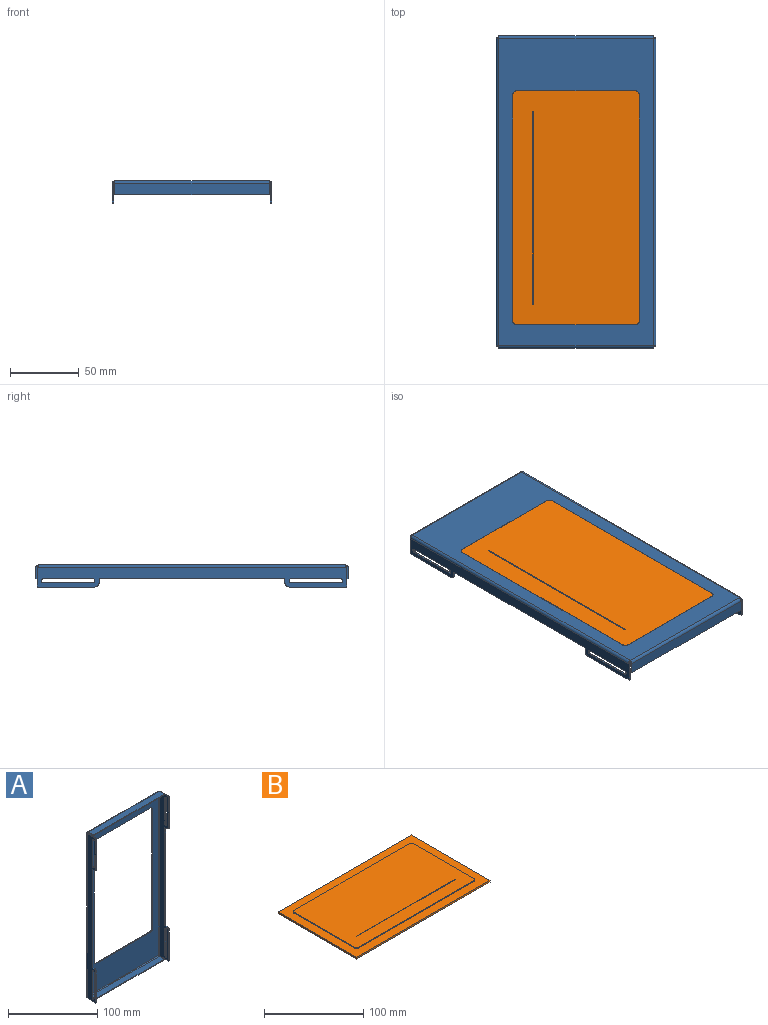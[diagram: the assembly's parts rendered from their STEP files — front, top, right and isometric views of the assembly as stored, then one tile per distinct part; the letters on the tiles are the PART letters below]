
ASSEMBLY  parts=2 mates=1
PART A: 78 faces, bbox 116x16x227 mm
  f0: cylinder r=3mm len=3mm, axis (0,1,0), area 4.7mm2, adj f1,f7,f8,f9
  f1: plane 86x1mm, normal (0,0,1), area 86mm2, adj f0,f2,f8,f9
  f2: cylinder r=3mm len=3mm, axis (0,1,0), area 4.7mm2, adj f1,f3,f8,f9
  f3: plane 164x1mm, normal (-1,0,0), area 164mm2, adj f2,f4,f8,f9
  f4: cylinder r=3mm len=3mm, axis (0,1,0), area 4.7mm2, adj f3,f5,f8,f9
  f5: plane 86x1mm, normal (0,0,-1), area 86mm2, adj f4,f6,f8,f9
  f6: cylinder r=3mm len=3mm, axis (0,1,0), area 4.7mm2, adj f5,f7,f8,f9
  f7: plane 164x1mm, normal (1,0,0), area 164mm2, adj f0,f6,f8,f9
  f8: plane 223x112mm, normal (0,1,0), area 9343.7mm2, adj f0,f1,f2,f3,f4,f5,f6,f7
  f9: plane 223x112mm, normal (0,-1,0), area 9343.7mm2, adj f0,f1,f2,f3,f4,f5,f6,f7
  f10: plane 1x1mm, normal (0,1,0), area 1mm2, adj f16,f29,f30,f32
  f11: plane 3x1mm, normal (0,0,1), area 3mm2, adj f12,f28,f29,f30
  f12: plane 135x1mm, normal (0,-1,0), area 135mm2, adj f11,f13,f29,f30
  f13: plane 3x1mm, normal (0,0,-1), area 3mm2, adj f12,f14,f29,f30
  f14: cylinder r=3mm len=3mm, axis (-1,0,0), area 4.7mm2, adj f13,f15,f29,f30
  f15: plane 42x1mm, normal (0,-1,0), area 42mm2, adj f14,f16,f29,f30
  f16: plane 14x1mm, normal (0,0,1), area 14mm2, adj f10,f15,f29,f30
  f17: plane 1x1mm, normal (0,1,0), area 1mm2, adj f18,f29,f30,f31
  f18: plane 14x1mm, normal (0,0,-1), area 14mm2, adj f17,f19,f29,f30
  f19: plane 42x1mm, normal (0,-1,0), area 42mm2, adj f18,f28,f29,f30
  f20: cylinder r=1.5mm len=3mm, axis (-1,0,0), area 4.7mm2, adj f21,f27,f29,f30
  f21: plane 36x1mm, normal (0,-1,0), area 36mm2, adj f20,f22,f29,f30
  f22: cylinder r=1.5mm len=3mm, axis (-1,0,0), area 4.7mm2, adj f21,f27,f29,f30
  f23: cylinder r=1.5mm len=3mm, axis (-1,0,0), area 4.7mm2, adj f24,f26,f29,f30
  f24: plane 36x1mm, normal (0,-1,0), area 36mm2, adj f23,f25,f29,f30
  f25: cylinder r=1.5mm len=3mm, axis (-1,0,0), area 4.7mm2, adj f24,f26,f29,f30
  f26: plane 36x1mm, normal (0,1,0), area 36mm2, adj f23,f25,f29,f30
  f27: plane 36x1mm, normal (0,1,0), area 36mm2, adj f20,f22,f29,f30
  f28: cylinder r=3mm len=3mm, axis (-1,0,0), area 4.7mm2, adj f11,f19,f29,f30
  f29: plane 225x14mm, normal (-1,0,0), area 2106mm2, adj f10,f11,f12,f13,f14,f15,f16,f17
  f30: plane 225x14mm, normal (1,0,0), area 2106mm2, adj f10,f11,f12,f13,f14,f15,f16,f17
  f31: plane 2x2mm, normal (0,0,-1), area 2.4mm2, adj f17,f33,f34,f65
  f32: plane 2x2mm, normal (0,0,1), area 2.4mm2, adj f10,f33,f34,f75
  f33: cylinder r=2mm len=223mm, axis (0,0,-1), area 700.6mm2, adj f8,f29,f31,f32
  f34: cylinder r=1mm len=223mm, axis (0,0,-1), area 350.3mm2, adj f9,f30,f31,f32
  f35: plane 1x1mm, normal (0,1,0), area 1mm2, adj f37,f54,f55,f57
  f36: plane 42x1mm, normal (0,-1,0), area 42mm2, adj f37,f53,f54,f55
  f37: plane 14x1mm, normal (0,0,-1), area 14mm2, adj f35,f36,f54,f55
  f38: plane 1x1mm, normal (0,1,0), area 1mm2, adj f39,f54,f55,f56
  f39: plane 14x1mm, normal (0,0,1), area 14mm2, adj f38,f40,f54,f55
  f40: plane 42x1mm, normal (0,-1,0), area 42mm2, adj f39,f41,f54,f55
  f41: cylinder r=3mm len=3mm, axis (1,0,0), area 4.7mm2, adj f40,f42,f54,f55
  f42: plane 3x1mm, normal (0,0,-1), area 3mm2, adj f41,f43,f54,f55
  f43: plane 135x1mm, normal (0,-1,0), area 135mm2, adj f42,f44,f54,f55
  f44: plane 3x1mm, normal (0,0,1), area 3mm2, adj f43,f53,f54,f55
  f45: cylinder r=1.5mm len=3mm, axis (1,0,0), area 4.7mm2, adj f46,f52,f54,f55
  f46: plane 36x1mm, normal (0,1,0), area 36mm2, adj f45,f47,f54,f55
  f47: cylinder r=1.5mm len=3mm, axis (1,0,0), area 4.7mm2, adj f46,f52,f54,f55
  f48: cylinder r=1.5mm len=3mm, axis (1,0,0), area 4.7mm2, adj f49,f51,f54,f55
  f49: plane 36x1mm, normal (0,1,0), area 36mm2, adj f48,f50,f54,f55
  f50: cylinder r=1.5mm len=3mm, axis (1,0,0), area 4.7mm2, adj f49,f51,f54,f55
  f51: plane 36x1mm, normal (0,-1,0), area 36mm2, adj f48,f50,f54,f55
  f52: plane 36x1mm, normal (0,-1,0), area 36mm2, adj f45,f47,f54,f55
  f53: cylinder r=3mm len=3mm, axis (1,0,0), area 4.7mm2, adj f36,f44,f54,f55
  f54: plane 225x14mm, normal (1,0,0), area 2106mm2, adj f35,f36,f37,f38,f39,f40,f41,f42
  f55: plane 225x14mm, normal (-1,0,0), area 2106mm2, adj f35,f36,f37,f38,f39,f40,f41,f42
  f56: plane 2x2mm, normal (0,0,1), area 2.4mm2, adj f38,f58,f59,f74
  f57: plane 2x2mm, normal (0,0,-1), area 2.4mm2, adj f35,f58,f59,f66
  f58: cylinder r=2mm len=223mm, axis (0,0,1), area 700.6mm2, adj f8,f54,f56,f57
  f59: cylinder r=1mm len=223mm, axis (0,0,1), area 350.3mm2, adj f9,f55,f56,f57
  f60: plane 8x1mm, normal (-1,0,0), area 8mm2, adj f62,f63,f64,f65
  f61: plane 8x1mm, normal (1,0,0), area 8mm2, adj f62,f63,f64,f66
  f62: plane 112x1mm, normal (0,-1,0), area 112mm2, adj f60,f61,f63,f64
  f63: plane 112x8mm, normal (0,0,-1), area 896mm2, adj f60,f61,f62,f67
  f64: plane 112x8mm, normal (0,0,1), area 896mm2, adj f60,f61,f62,f68
  f65: plane 2x2mm, normal (-1,0,0), area 2.4mm2, adj f31,f60,f67,f68
  f66: plane 2x2mm, normal (1,0,0), area 2.4mm2, adj f57,f61,f67,f68
  f67: cylinder r=2mm len=112mm, axis (-1,0,0), area 351.9mm2, adj f8,f63,f65,f66
  f68: cylinder r=1mm len=112mm, axis (-1,0,0), area 175.9mm2, adj f9,f64,f65,f66
  f69: plane 8x1mm, normal (1,0,0), area 8mm2, adj f71,f72,f73,f74
  f70: plane 8x1mm, normal (-1,0,0), area 8mm2, adj f71,f72,f73,f75
  f71: plane 112x1mm, normal (0,-1,0), area 112mm2, adj f69,f70,f72,f73
  f72: plane 112x8mm, normal (0,0,1), area 896mm2, adj f69,f70,f71,f76
  f73: plane 112x8mm, normal (0,0,-1), area 896mm2, adj f69,f70,f71,f77
  f74: plane 2x2mm, normal (1,0,0), area 2.4mm2, adj f56,f69,f76,f77
  f75: plane 2x2mm, normal (-1,0,0), area 2.4mm2, adj f32,f70,f76,f77
  f76: cylinder r=2mm len=112mm, axis (1,0,0), area 351.9mm2, adj f8,f72,f74,f75
  f77: cylinder r=1mm len=112mm, axis (1,0,0), area 175.9mm2, adj f9,f73,f74,f75
PART B: 27 faces, bbox 190x112x3 mm
  f0: plane 190x2mm, normal (0,-1,0), area 380mm2, adj f1,f3,f4,f13
  f1: plane 112x2mm, normal (1,0,0), area 224mm2, adj f0,f2,f4,f13
  f2: plane 190x2mm, normal (0,1,0), area 380mm2, adj f1,f3,f4,f13
  f3: plane 112x2mm, normal (-1,0,0), area 224mm2, adj f0,f2,f4,f13
  f4: plane 190x112mm, normal (0,0,-1), area 21280mm2, adj f0,f1,f2,f3
  f5: cylinder r=3mm len=3mm, axis (0,0,1), area 4.2mm2, adj f6,f12,f13,f22
  f6: plane 164x0.9mm, normal (0,-1,0), area 147.6mm2, adj f5,f7,f13,f20
  f7: cylinder r=3mm len=3mm, axis (0,0,1), area 4.2mm2, adj f6,f8,f13,f18
  f8: plane 86x0.9mm, normal (-1,0,0), area 77.4mm2, adj f7,f9,f13,f16
  f9: cylinder r=3mm len=3mm, axis (0,0,1), area 4.2mm2, adj f8,f10,f13,f15
  f10: plane 164x0.9mm, normal (0,1,0), area 147.6mm2, adj f9,f11,f13,f17
  f11: cylinder r=3mm len=3mm, axis (0,0,1), area 4.2mm2, adj f10,f12,f13,f19
  f12: plane 86x0.9mm, normal (1,0,0), area 77.4mm2, adj f5,f11,f13,f21
  f13: plane 190x112mm, normal (0,0,1), area 5647.7mm2, adj f0,f1,f2,f3,f5,f6,f7,f8
  f14: plane 169.8x91.8mm, normal (0,0,1), area 15499.6mm2, adj f15,f16,f17,f18,f19,f20,f21,f22
  f15: cone r=2.9mm half-angle=45deg, axis (0,0,-1), area 0.7mm2, adj f9,f14,f16,f17
  f16: plane 86x0.1mm, normal (-0.71,0,0.71), area 12.2mm2, adj f8,f14,f15,f18
  f17: plane 164x0.1mm, normal (0,0.71,0.71), area 23.2mm2, adj f10,f14,f15,f19
  f18: cone r=2.9mm half-angle=45deg, axis (0,0,-1), area 0.7mm2, adj f7,f14,f16,f20
  f19: cone r=2.9mm half-angle=45deg, axis (0,0,-1), area 0.7mm2, adj f11,f14,f17,f21
  f20: plane 164x0.1mm, normal (0,-0.71,0.71), area 23.2mm2, adj f6,f14,f18,f22
  f21: plane 86x0.1mm, normal (0.71,0,0.71), area 12.2mm2, adj f12,f14,f19,f22
  f22: cone r=2.9mm half-angle=45deg, axis (0,0,-1), area 0.7mm2, adj f5,f14,f20,f21
  f23: plane 140x0.5mm, normal (0,0.87,0.5), area 80.8mm2, adj f14,f24,f25,f26
  f24: plane 140x0.5mm, normal (0,-0.87,0.5), area 80.8mm2, adj f14,f23,f25,f26
  f25: plane 0.58x0.5mm, normal (-1,0,0), area 0.1mm2, adj f14,f23,f24
  f26: plane 0.58x0.5mm, normal (1,0,0), area 0.1mm2, adj f14,f23,f24
PLACE A rot(axis=(1,0,0),90deg) t=(-104.5,-61.94,109.22)mm
PLACE B rot(axis=(0,0,-1),90deg) t=(-104.5,-185.94,146.72)mm
MATE fastened B.f7 <-> A.f0  axis (0,0,1) through (-147.5,-103.94,148.72)mm
